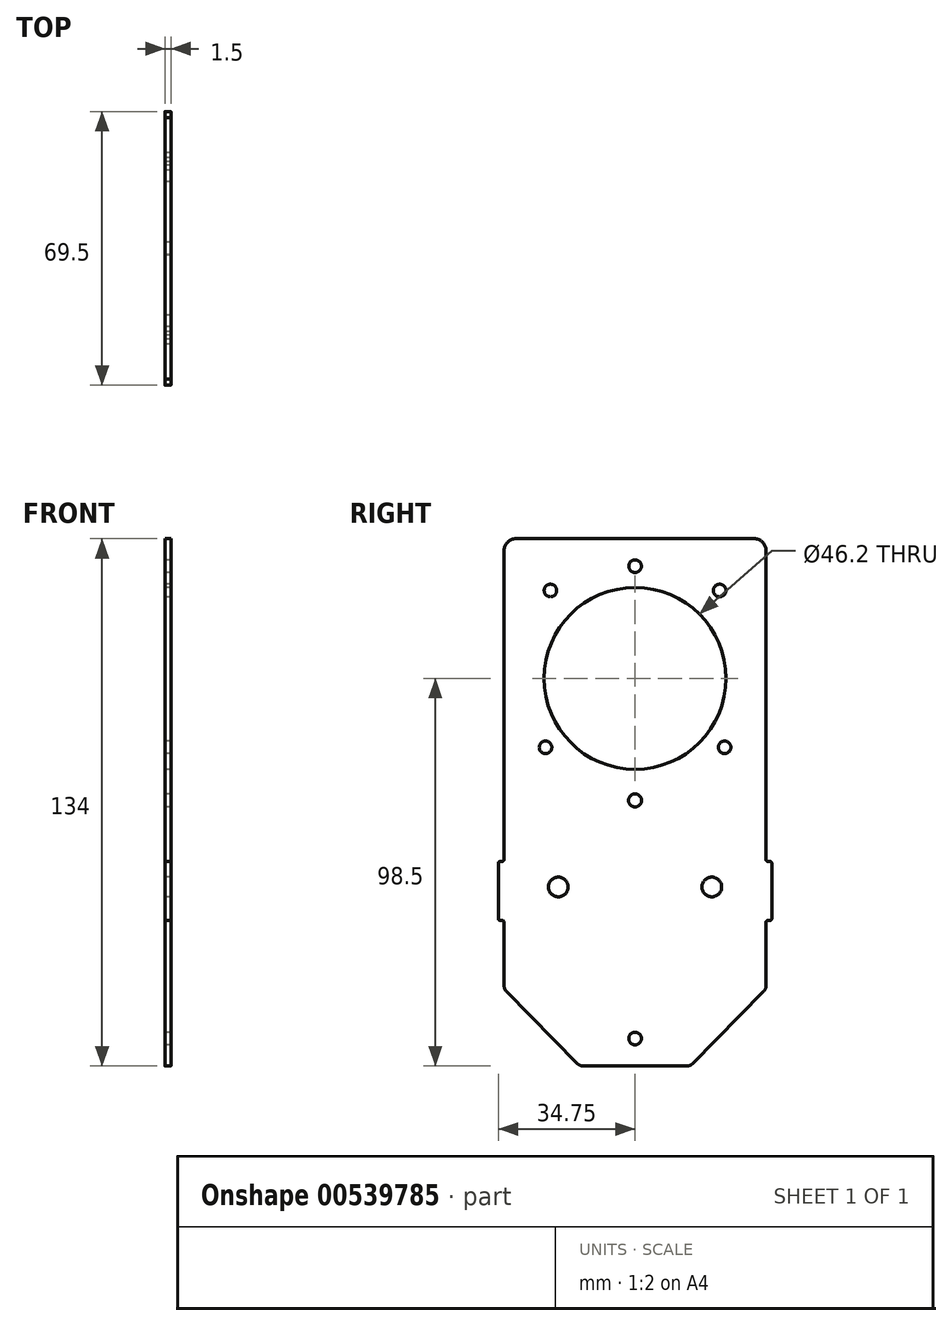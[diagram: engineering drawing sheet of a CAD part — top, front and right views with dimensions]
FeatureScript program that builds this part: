
annotation { "Feature Type Name" : "Feature", "Feature Type Description" : "" }
export const myFeature = defineFeature(function(context is Context, id is Id, definition is map)
    precondition{}
    {
        {
            var Q0;
            Q0=qCreatedBy(makeId("Right.planeOp"),FACE);
            var sketch = newSketch(context, id + "F0", { "sketchPlane" : qUnion([Q0])});
            skLineSegment(sketch, "E0.bottom", {"start": v(30.25, 67) * mm, "end": v(-30.25, 67) * mm});
            skLineSegment(sketch, "E0.top", {"start": v(13.16, -67) * mm, "end": v(-13.16, -67) * mm});
            skLineSegment(sketch, "E0.left", {"start": v(33.25, 64) * mm, "end": v(33.25, -14.5) * mm});
            skLineSegment(sketch, "E0.right", {"start": v(-33.25, 64) * mm, "end": v(-33.25, -14.5) * mm});
            skPoint(sketch, "E0.middle", {"position": v(0, 0) * mm});
            skCircle(sketch, "E1", {"center": v(0, 31.5) * mm, "radius": 23.1 * mm});
            skCircle(sketch, "E2", {"center": v(-21.5, 53.83) * mm, "radius": 1.6 * mm});
            skCircle(sketch, "E3", {"center": v(21.5, 53.83) * mm, "radius": 1.6 * mm});
            skCircle(sketch, "E4", {"center": v(0, 0.5) * mm, "radius": 1.65 * mm});
            skCircle(sketch, "E5", {"center": v(-19.5, -21.5) * mm, "radius": 2.5 * mm});
            skCircle(sketch, "E6", {"center": v(19.5, -21.5) * mm, "radius": 2.5 * mm});
            skCircle(sketch, "E7", {"center": v(0, -60) * mm, "radius": 1.6 * mm});
            skPoint(sketch, "E8.visualSharp", {"position": v(-33.25, 67) * mm});
            skArc(sketch, "E8.filletArc", {"start": v(-30.25, 67) * mm, "mid": v(-32.37, 66.12) * mm, "end": v(-33.25, 64) * mm});
            skPoint(sketch, "E9.visualSharp", {"position": v(33.25, 67) * mm});
            skArc(sketch, "E9.filletArc", {"start": v(33.25, 64) * mm, "mid": v(32.37, 66.12) * mm, "end": v(30.25, 67) * mm});
            skLineSegment(sketch, "E10", {"start": v(-14.59, -66.4) * mm, "end": v(-32.67, -48.08) * mm});
            skLineSegment(sketch, "E11", {"start": v(32.67, -48.08) * mm, "end": v(14.59, -66.4) * mm});
            skPoint(sketch, "E12.bottom.start.orphan", {"position": v(-33.25, -67) * mm});
            skPoint(sketch, "E13.bottom.start.orphan", {"position": v(33.25, -67) * mm});
            skPoint(sketch, "E14.visualSharp", {"position": v(-33.25, -47.5) * mm});
            skArc(sketch, "E14.filletArc", {"start": v(-33.25, -46.68) * mm, "mid": v(-33.1, -47.44) * mm, "end": v(-32.67, -48.08) * mm});
            skPoint(sketch, "E15.visualSharp", {"position": v(-14, -67) * mm});
            skArc(sketch, "E15.filletArc", {"start": v(-14.59, -66.4) * mm, "mid": v(-13.94, -66.85) * mm, "end": v(-13.16, -67) * mm});
            skPoint(sketch, "E16.visualSharp", {"position": v(14, -67) * mm});
            skArc(sketch, "E16.filletArc", {"start": v(13.16, -67) * mm, "mid": v(13.94, -66.85) * mm, "end": v(14.59, -66.4) * mm});
            skPoint(sketch, "E17.visualSharp", {"position": v(33.25, -47.5) * mm});
            skArc(sketch, "E17.filletArc", {"start": v(32.67, -48.08) * mm, "mid": v(33.1, -47.44) * mm, "end": v(33.25, -46.68) * mm});
            skLineSegment(sketch, "E18.bottom", {"start": v(33.75, -15) * mm, "end": v(34.25, -15) * mm});
            skLineSegment(sketch, "E18.top", {"start": v(33.75, -30) * mm, "end": v(34.25, -30) * mm});
            skLineSegment(sketch, "E18.right", {"start": v(34.75, -15.5) * mm, "end": v(34.75, -29.5) * mm});
            skLineSegment(sketch, "E19.bottom", {"start": v(-33.75, -15) * mm, "end": v(-34.25, -15) * mm});
            skLineSegment(sketch, "E19.top", {"start": v(-33.75, -30) * mm, "end": v(-34.25, -30) * mm});
            skLineSegment(sketch, "E19.right", {"start": v(-34.75, -15.5) * mm, "end": v(-34.75, -29.5) * mm});
            skPoint(sketch, "E20.visualSharp", {"position": v(-34.75, -30) * mm});
            skArc(sketch, "E20.filletArc", {"start": v(-34.75, -29.5) * mm, "mid": v(-34.6, -29.85) * mm, "end": v(-34.25, -30) * mm});
            skPoint(sketch, "E21.visualSharp", {"position": v(-34.75, -15) * mm});
            skArc(sketch, "E21.filletArc", {"start": v(-34.25, -15) * mm, "mid": v(-34.6, -15.15) * mm, "end": v(-34.75, -15.5) * mm});
            skPoint(sketch, "E22.visualSharp", {"position": v(34.75, -15) * mm});
            skArc(sketch, "E22.filletArc", {"start": v(34.75, -15.5) * mm, "mid": v(34.6, -15.15) * mm, "end": v(34.25, -15) * mm});
            skPoint(sketch, "E23.visualSharp", {"position": v(34.75, -30) * mm});
            skArc(sketch, "E23.filletArc", {"start": v(34.25, -30) * mm, "mid": v(34.6, -29.85) * mm, "end": v(34.75, -29.5) * mm});
            skPoint(sketch, "E24.newPointB", {"position": v(33.25, -15) * mm});
            skArc(sketch, "E24.filletArc", {"start": v(33.25, -14.5) * mm, "mid": v(33.4, -14.85) * mm, "end": v(33.75, -15) * mm});
            skPoint(sketch, "E25.newPointA", {"position": v(-33.25, -15) * mm});
            skArc(sketch, "E25.filletArc", {"start": v(-33.75, -15) * mm, "mid": v(-33.4, -14.85) * mm, "end": v(-33.25, -14.5) * mm});
            skLineSegment(sketch, "E26", {"start": v(-33.25, -46.68) * mm, "end": v(-33.25, -30.5) * mm});
            skLineSegment(sketch, "E27", {"start": v(33.25, -30.5) * mm, "end": v(33.25, -46.68) * mm});
            skPoint(sketch, "E28.visualSharp", {"position": v(-33.25, -30) * mm});
            skArc(sketch, "E28.filletArc", {"start": v(-33.25, -30.5) * mm, "mid": v(-33.4, -30.15) * mm, "end": v(-33.75, -30) * mm});
            skPoint(sketch, "E29.visualSharp", {"position": v(33.25, -30) * mm});
            skArc(sketch, "E29.filletArc", {"start": v(33.75, -30) * mm, "mid": v(33.4, -30.15) * mm, "end": v(33.25, -30.5) * mm});
            skCircle(sketch, "E30", {"center": v(22.75, 14) * mm, "radius": 1.6 * mm});
            skCircle(sketch, "E31", {"center": v(-22.75, 14) * mm, "radius": 1.6 * mm});
            skCircle(sketch, "E32", {"center": v(0, 60) * mm, "radius": 1.6 * mm});
            skSolve(sketch);
        }
        {
            var Q0;
            Q0 = qSketchRegion(id + "F0", true);
            extrude(context, id + "F1", {"entities" : qUnion([Q0]), "depth" : 1.5 * mm, "offsetDistance" : 25 * mm});
        }
    });
